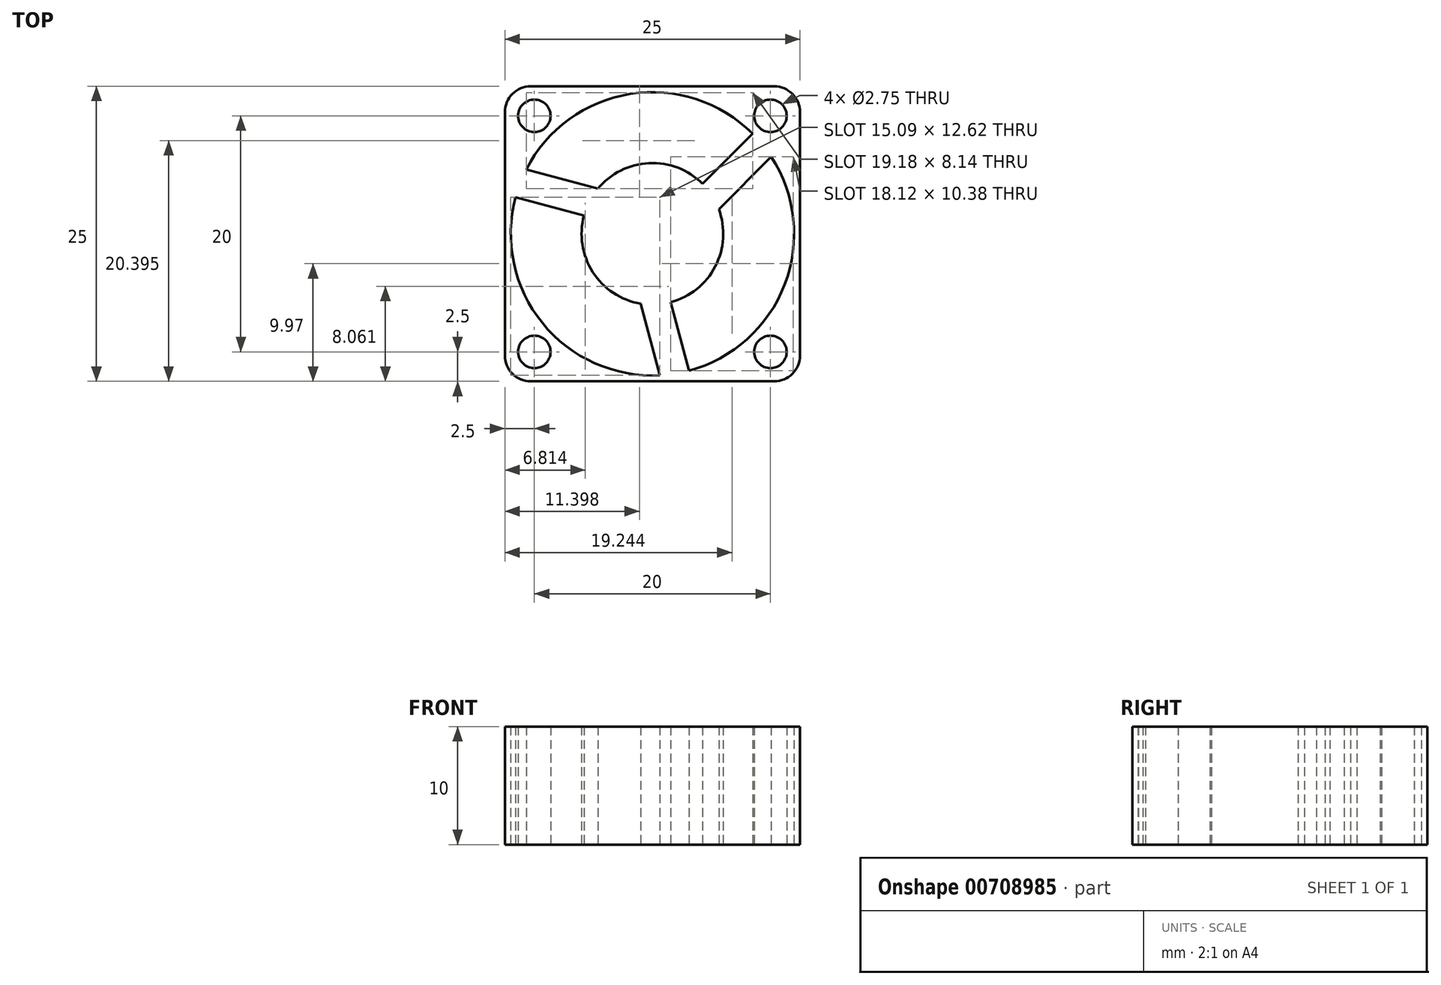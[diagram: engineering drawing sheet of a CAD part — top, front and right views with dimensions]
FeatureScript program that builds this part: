
annotation { "Feature Type Name" : "Feature", "Feature Type Description" : "" }
export const myFeature = defineFeature(function(context is Context, id is Id, definition is map)
    precondition{}
    {
        {
            var Q0;
            Q0=qCreatedBy(makeId("Top.planeOp"),FACE);
            var sketch = newSketch(context, id + "F0", { "sketchPlane" : qUnion([Q0])});
            skLineSegment(sketch, "E0.bottom", {"start": v(10.3, -12.5) * mm, "end": v(-10.3, -12.5) * mm});
            skLineSegment(sketch, "E0.top", {"start": v(10.3, 12.5) * mm, "end": v(-10.3, 12.5) * mm});
            skLineSegment(sketch, "E0.left", {"start": v(12.5, -10.3) * mm, "end": v(12.5, 10.3) * mm});
            skLineSegment(sketch, "E0.right", {"start": v(-12.5, -10.3) * mm, "end": v(-12.5, 10.3) * mm});
            skPoint(sketch, "E0.middle", {"position": v(0, 0) * mm});
            skCircle(sketch, "E1", {"center": v(0, 0) * mm, "radius": 12 * mm});
            skCircle(sketch, "E2", {"center": v(-10, 10) * mm, "radius": 1.38 * mm});
            skCircle(sketch, "E3", {"center": v(10, 10) * mm, "radius": 1.38 * mm});
            skCircle(sketch, "E4", {"center": v(10, -10) * mm, "radius": 1.38 * mm});
            skCircle(sketch, "E5", {"center": v(-10, -10) * mm, "radius": 1.38 * mm});
            skLineSegment(sketch, "E6", {"start": v(-12.5, -12.5) * mm, "end": v(12.5, 12.5) * mm});
            skLineSegment(sketch, "E7", {"start": v(-12.5, 12.5) * mm, "end": v(12.5, -12.5) * mm});
            skPoint(sketch, "E8.visualSharp", {"position": v(-12.5, 12.5) * mm});
            skArc(sketch, "E8.filletArc", {"start": v(-10.3, 12.5) * mm, "mid": v(-11.86, 11.86) * mm, "end": v(-12.5, 10.3) * mm});
            skPoint(sketch, "E9.visualSharp", {"position": v(12.5, 12.5) * mm});
            skArc(sketch, "E9.filletArc", {"start": v(12.5, 10.3) * mm, "mid": v(11.86, 11.86) * mm, "end": v(10.3, 12.5) * mm});
            skPoint(sketch, "E10.visualSharp", {"position": v(12.5, -12.5) * mm});
            skArc(sketch, "E10.filletArc", {"start": v(10.3, -12.5) * mm, "mid": v(11.86, -11.86) * mm, "end": v(12.5, -10.3) * mm});
            skPoint(sketch, "E11.visualSharp", {"position": v(-12.5, -12.5) * mm});
            skArc(sketch, "E11.filletArc", {"start": v(-12.5, -10.3) * mm, "mid": v(-11.86, -11.86) * mm, "end": v(-10.3, -12.5) * mm});
            skLineSegment(sketch, "E12", {"start": v(0, 0) * mm, "end": v(-11.6, 3.1) * mm});
            skLineSegment(sketch, "E13", {"start": v(0, 0) * mm, "end": v(3.1, -11.6) * mm});
            skCircle(sketch, "E14", {"center": v(0, 0) * mm, "radius": 6 * mm});
            skLineSegment(sketch, "E15", {"start": v(-10.69, 5.45) * mm, "end": v(-4.62, 3.83) * mm});
            skLineSegment(sketch, "E16", {"start": v(5.62, 2.09) * mm, "end": v(10.07, 6.53) * mm});
            skLineSegment(sketch, "E17", {"start": v(-1, -5.92) * mm, "end": v(0.62, -11.98) * mm});
            skSolve(sketch);
        }
        {
            var Q0;
            {var subQ4=sQuery(id+"F0.wireOp",EDGE,"E0.right");Q0=makeQuery(id+"F0.imprint","IMPRINT",FACE,{"disambiguationData":[TD([[makeQuery(id+"F0.imprint","IMPRINT",EDGE,{"derivedFrom":subQ4}),-1.0]])]});}
            var Q1;
            {var subQ9=sQuery(id+"F0.wireOp",EDGE,"E0.bottom");Q1=makeQuery(id+"F0.imprint","IMPRINT",FACE,{"disambiguationData":[TD([[makeQuery(id+"F0.imprint","IMPRINT",EDGE,{"derivedFrom":subQ9}),-1.0]])]});}
            var Q2;
            {var subQ4=sQuery(id+"F0.wireOp",EDGE,"E0.left");Q2=makeQuery(id+"F0.imprint","IMPRINT",FACE,{"disambiguationData":[TD([[makeQuery(id+"F0.imprint","IMPRINT",EDGE,{"derivedFrom":subQ4}),1.0]])]});}
            var Q3;
            {var subQ7=sQuery(id+"F0.wireOp",EDGE,"E0.top");Q3=makeQuery(id+"F0.imprint","IMPRINT",FACE,{"disambiguationData":[TD([[makeQuery(id+"F0.imprint","IMPRINT",EDGE,{"derivedFrom":subQ7}),1.0]])]});}
            var Q4;
            {var subQ3=sQuery(id+"F0.wireOp",EDGE,"E15");Q4=makeQuery(id+"F0.imprint","IMPRINT",FACE,{"disambiguationData":[TD([[makeQuery(id+"F0.imprint","IMPRINT",EDGE,{"derivedFrom":subQ3}),-1.0]])]});}
            var Q5;
            {var subQ3=sQuery(id+"F0.wireOp",EDGE,"E14");var subQ5=makeQuery(id+"F0.imprint","INTERSECT",VERTEX,{"derivedFrom":[subQ3,sQuery(id+"F0.wireOp",EDGE,"E15")]});Q5=makeQuery(id+"F0.imprint","IMPRINT",FACE,{"disambiguationData":[TD([[makeQuery(id+"F0.imprint","IMPRINT",EDGE,{"disambiguationData":[TD([[subQ5,1.0]])],"derivedFrom":subQ3}),1.0]])]});}
            var Q6;
            {var subQ1=sQuery(id+"F0.wireOp",EDGE,"E6");var subQ3=sQuery(id+"F0.wireOp",EDGE,"E14");var subQ4=makeQuery(id+"F0.imprint","INTERSECT",VERTEX,{"disambiguationData":[OD(1.0)],"derivedFrom":[subQ1,subQ3]});Q6=makeQuery(id+"F0.imprint","IMPRINT",FACE,{"disambiguationData":[TD([[makeQuery(id+"F0.imprint","IMPRINT",EDGE,{"disambiguationData":[TD([[subQ4,-1.0]])],"derivedFrom":subQ3}),1.0]])]});}
            var Q7;
            {var subQ3=sQuery(id+"F0.wireOp",EDGE,"E14");var subQ6=makeQuery(id+"F0.imprint","INTERSECT",VERTEX,{"derivedFrom":[subQ3,sQuery(id+"F0.wireOp",EDGE,"E16")]});Q7=makeQuery(id+"F0.imprint","IMPRINT",FACE,{"disambiguationData":[TD([[makeQuery(id+"F0.imprint","IMPRINT",EDGE,{"disambiguationData":[TD([[subQ6,-1.0]])],"derivedFrom":subQ3}),1.0]])]});}
            var Q8;
            {var subQ0=sQuery(id+"F0.wireOp",EDGE,"E16");Q8=makeQuery(id+"F0.imprint","IMPRINT",FACE,{"disambiguationData":[TD([[makeQuery(id+"F0.imprint","IMPRINT",EDGE,{"derivedFrom":subQ0}),1.0]])]});}
            var Q9;
            {var subQ1=sQuery(id+"F0.wireOp",EDGE,"E7");var subQ3=sQuery(id+"F0.wireOp",EDGE,"E14");var subQ4=makeQuery(id+"F0.imprint","INTERSECT",VERTEX,{"disambiguationData":[OD(1.0)],"derivedFrom":[subQ1,subQ3]});Q9=makeQuery(id+"F0.imprint","IMPRINT",FACE,{"disambiguationData":[TD([[makeQuery(id+"F0.imprint","IMPRINT",EDGE,{"disambiguationData":[TD([[subQ4,1.0]])],"derivedFrom":subQ3}),1.0]])]});}
            var Q10;
            {var subQ3=sQuery(id+"F0.wireOp",EDGE,"E14");var subQ6=makeQuery(id+"F0.imprint","INTERSECT",VERTEX,{"derivedFrom":[subQ3,sQuery(id+"F0.wireOp",EDGE,"E17")]});Q10=makeQuery(id+"F0.imprint","IMPRINT",FACE,{"disambiguationData":[TD([[makeQuery(id+"F0.imprint","IMPRINT",EDGE,{"disambiguationData":[TD([[subQ6,1.0]])],"derivedFrom":subQ3}),1.0]])]});}
            var Q11;
            {var subQ1=sQuery(id+"F0.wireOp",EDGE,"E6");var subQ3=sQuery(id+"F0.wireOp",EDGE,"E14");var subQ4=makeQuery(id+"F0.imprint","INTERSECT",VERTEX,{"disambiguationData":[OD(0.0)],"derivedFrom":[subQ1,subQ3]});Q11=makeQuery(id+"F0.imprint","IMPRINT",FACE,{"disambiguationData":[TD([[makeQuery(id+"F0.imprint","IMPRINT",EDGE,{"disambiguationData":[TD([[subQ4,1.0]])],"derivedFrom":subQ3}),1.0]])]});}
            var Q12;
            {var subQ3=sQuery(id+"F0.wireOp",EDGE,"E17");Q12=makeQuery(id+"F0.imprint","IMPRINT",FACE,{"disambiguationData":[TD([[makeQuery(id+"F0.imprint","IMPRINT",EDGE,{"derivedFrom":subQ3}),1.0]])]});}
            extrude(context, id + "F1", {"entities" : qUnion([Q0, Q1, Q2, Q3, Q4, Q5, Q6, Q7, Q8, Q9, Q10, Q11, Q12]), "depth" : 10 * mm, "offsetDistance" : 25 * mm});
        }
    });
